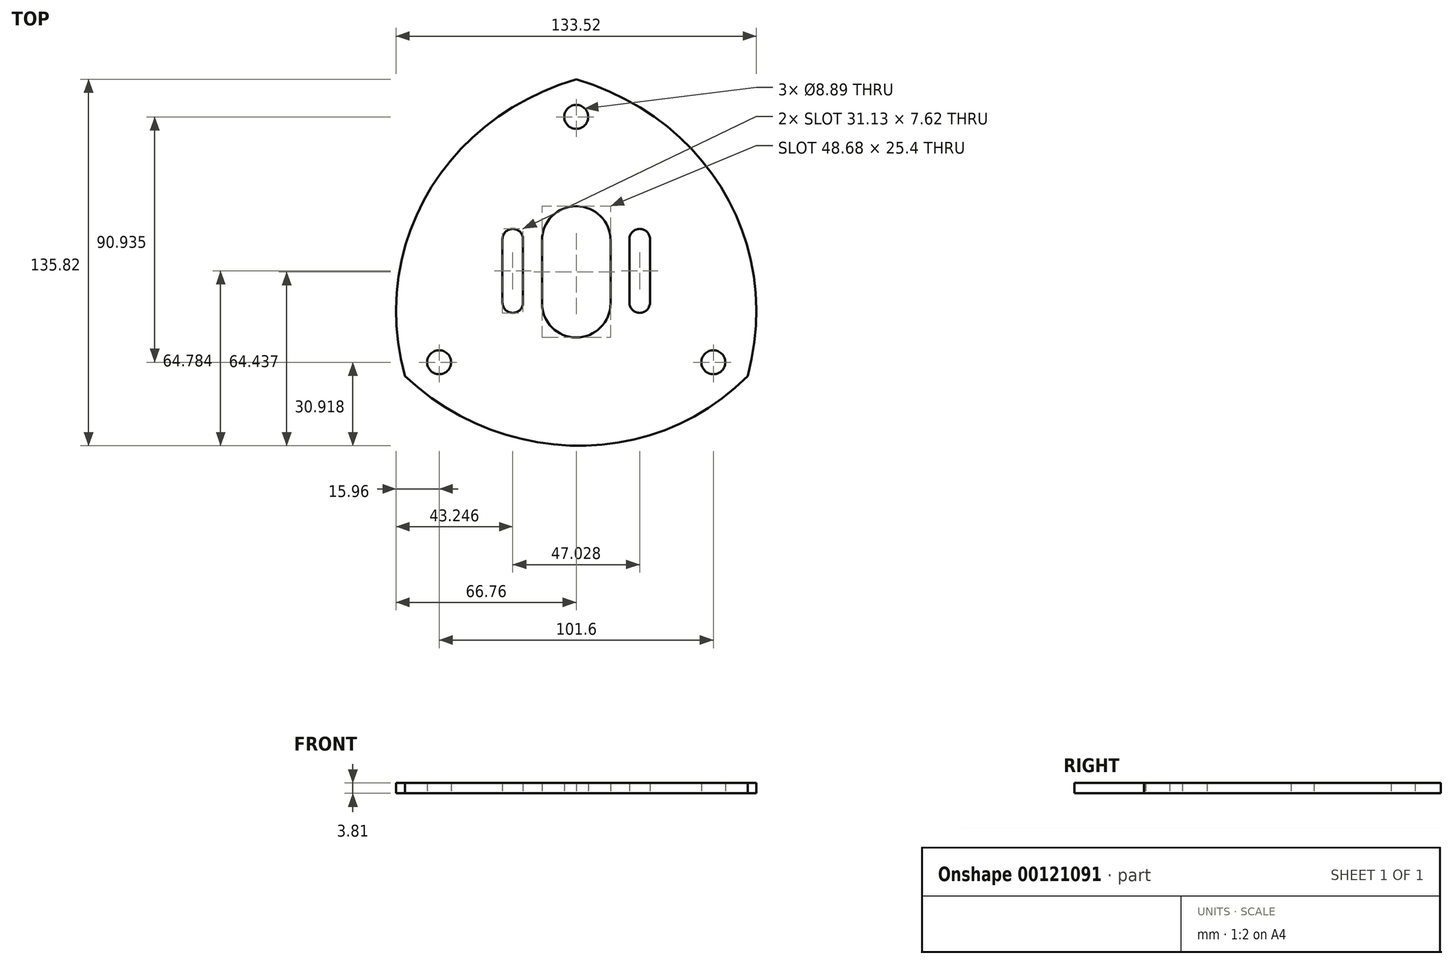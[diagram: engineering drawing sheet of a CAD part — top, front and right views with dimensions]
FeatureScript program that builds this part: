
annotation { "Feature Type Name" : "Feature", "Feature Type Description" : "" }
export const myFeature = defineFeature(function(context is Context, id is Id, definition is map)
    precondition{}
    {
        {
            var Q0;
            Q0=qCreatedBy(makeId("Top.planeOp"),FACE);
            var sketch = newSketch(context, id + "F0", { "sketchPlane" : qUnion([Q0])});
            skLineSegment(sketch, "E0", {"start": v(0, 40.33) * mm, "end": v(-63.5, -69.65) * mm});
            skLineSegment(sketch, "E1", {"start": v(-63.5, -69.65) * mm, "end": v(63.5, -69.65) * mm});
            skLineSegment(sketch, "E2", {"start": v(63.5, -69.65) * mm, "end": v(0, 40.33) * mm});
            skFitSpline(sketch, "E3", {"points": [v(0, 40.33) * mm, v(-63.5, -69.65) * mm], "startDerivative": vector(-148.04, -44.28) * mm, "endDerivative": vector(39.18, -144.03) * mm});
            skLineSegment(sketch, "E4", {"start": v(0, 40.33) * mm, "end": v(0, -69.65) * mm, "construction": true});
            skFitSpline(sketch, "E5", {"points": [v(-63.5, -69.65) * mm, v(63.5, -69.65) * mm], "startDerivative": vector(108.37, -101.88) * mm, "endDerivative": vector(103.45, 104.83) * mm});
            skFitSpline(sketch, "E6.MirrorCS", {"points": [v(0, 40.33) * mm, v(63.5, -69.65) * mm], "startDerivative": vector(148.04, -44.28) * mm, "endDerivative": vector(-39.18, -144.03) * mm});
            skLineSegment(sketch, "E7.bottom", {"start": v(12.7, -19.41) * mm, "end": v(-12.7, -19.41) * mm});
            skLineSegment(sketch, "E7.top", {"start": v(12.7, -42.7) * mm, "end": v(-12.7, -42.7) * mm});
            skLineSegment(sketch, "E7.left", {"start": v(12.7, -19.41) * mm, "end": v(12.7, -42.7) * mm});
            skLineSegment(sketch, "E7.right", {"start": v(-12.7, -19.41) * mm, "end": v(-12.7, -42.7) * mm});
            skPoint(sketch, "E8", {"position": v(0, -18.42) * mm});
            skPoint(sketch, "E8.positionSnap0", {"position": v(0, -19.41) * mm});
            skArc(sketch, "E9", {"start": v(12.7, -19.41) * mm, "mid": v(0, -6.71) * mm, "end": v(-12.7, -19.41) * mm});
            skArc(sketch, "E10", {"start": v(-12.7, -42.7) * mm, "mid": v(0, -55.4) * mm, "end": v(12.7, -42.7) * mm});
            skCircle(sketch, "E11", {"center": v(0, 26.36) * mm, "radius": 4.45 * mm});
            skCircle(sketch, "E12", {"center": v(50.8, -64.57) * mm, "radius": 4.45 * mm});
            skCircle(sketch, "E13.MirrorC", {"center": v(-50.8, -64.57) * mm, "radius": 4.45 * mm});
            skLineSegment(sketch, "E14.bottom", {"start": v(-19.7, -42.46) * mm, "end": v(-27.32, -42.46) * mm});
            skLineSegment(sketch, "E14.top", {"start": v(-19.7, -18.95) * mm, "end": v(-27.32, -18.95) * mm});
            skLineSegment(sketch, "E14.left", {"start": v(-19.7, -42.46) * mm, "end": v(-19.7, -18.95) * mm});
            skLineSegment(sketch, "E14.right", {"start": v(-27.32, -42.46) * mm, "end": v(-27.32, -18.95) * mm});
            skLineSegment(sketch, "E15.MirrorCS", {"start": v(19.7, -18.95) * mm, "end": v(27.32, -18.95) * mm});
            skLineSegment(sketch, "E16.MirrorCS", {"start": v(27.32, -42.46) * mm, "end": v(27.32, -18.95) * mm});
            skLineSegment(sketch, "E17.MirrorCS", {"start": v(19.7, -42.46) * mm, "end": v(19.7, -18.95) * mm});
            skLineSegment(sketch, "E18.MirrorCS", {"start": v(19.7, -42.46) * mm, "end": v(27.32, -42.46) * mm});
            skArc(sketch, "E19", {"start": v(-27.32, -42.46) * mm, "mid": v(-23.51, -46.27) * mm, "end": v(-19.7, -42.46) * mm});
            skArc(sketch, "E20", {"start": v(-19.7, -18.95) * mm, "mid": v(-23.51, -15.14) * mm, "end": v(-27.32, -18.95) * mm});
            skArc(sketch, "E21.MirrorCS", {"start": v(19.7, -18.95) * mm, "mid": v(23.51, -15.14) * mm, "end": v(27.32, -18.95) * mm});
            skArc(sketch, "E22.MirrorCS", {"start": v(27.32, -42.46) * mm, "mid": v(23.51, -46.27) * mm, "end": v(19.7, -42.46) * mm});
            skSolve(sketch);
        }
        {
            var Q0;
            Q0=makeQuery(id+"F0.imprint","IMPRINT",FACE,{"disambiguationData":[TD([[makeQuery(id+"F0.imprint","IMPRINT",EDGE,{"derivedFrom":sQuery(id+"F0.wireOp",EDGE,"E1")}),-1.0]])]});
            var Q1;
            Q1=makeQuery(id+"F0.imprint","IMPRINT",FACE,{"disambiguationData":[TD([[makeQuery(id+"F0.imprint","IMPRINT",EDGE,{"derivedFrom":sQuery(id+"F0.wireOp",EDGE,"E2")}),-1.0]])]});
            var Q2;
            Q2=makeQuery(id+"F0.imprint","IMPRINT",FACE,{"disambiguationData":[TD([[makeQuery(id+"F0.imprint","IMPRINT",EDGE,{"derivedFrom":sQuery(id+"F0.wireOp",EDGE,"E0")}),1.0]])]});
            var Q3;
            Q3=makeQuery(id+"F0.imprint","IMPRINT",FACE,{"disambiguationData":[TD([[makeQuery(id+"F0.imprint","IMPRINT",EDGE,{"derivedFrom":sQuery(id+"F0.wireOp",EDGE,"E0")}),-1.0]])]});
            extrude(context, id + "F1", {"entities" : qUnion([Q0, Q1, Q2, Q3]), "depth" : 3.8 * mm});
        }
    });
